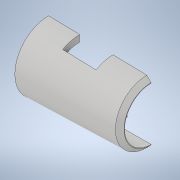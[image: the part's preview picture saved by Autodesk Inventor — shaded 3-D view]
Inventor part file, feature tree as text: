
AUTODESK INVENTOR PART (.ipt)
format: ipt  version: 2020 (Build 240168000, 168)  size: 161,792 bytes
history: native  units: mm
features: sketch x3, extrude x2, revolve x1, chamfer x1
ambient origin geometry x8: Origin, YZ Plane, XZ Plane, XY Plane, X Axis, Y Axis, Z Axis, Center Point
bodies: Solid1 (feature_tree)
feature tree (7):
  revolve  "Revolution1"  [1 undecoded]
  extrude  "Extrusion1"  Depth=200.0mm TaperAngle=0.0deg
  extrude  "Extrusion2"  Depth=11.85mm
  chamfer  "Chamfer1"  Distance=6.0mm
  sketch  "Sketch2"  dims[d2=36.35mm d3=9.7mm]
  sketch  "Sketch3"  dims[d9=270.0deg d17=200.0mm d18=0.0mm]
  sketch  "Sketch4"  dims[d21=11.0mm d23=5.0mm d24=6.0mm d25=11.0mm d27=200.0mm d28=0.0mm d31=1.5mm d32=2.0mm d33=45.0deg d34=0.2mm d36=0.5mm d39=2.6mm d40=1.7mm d41=9.4mm d43=11.85mm d44=11.85mm d45=11.35mm]
note: 1 required parameter value undecoded (feature->parameter linkage not recoverable at this tier; creation-order binding heuristic only, values carry confidence <= 0.55)
